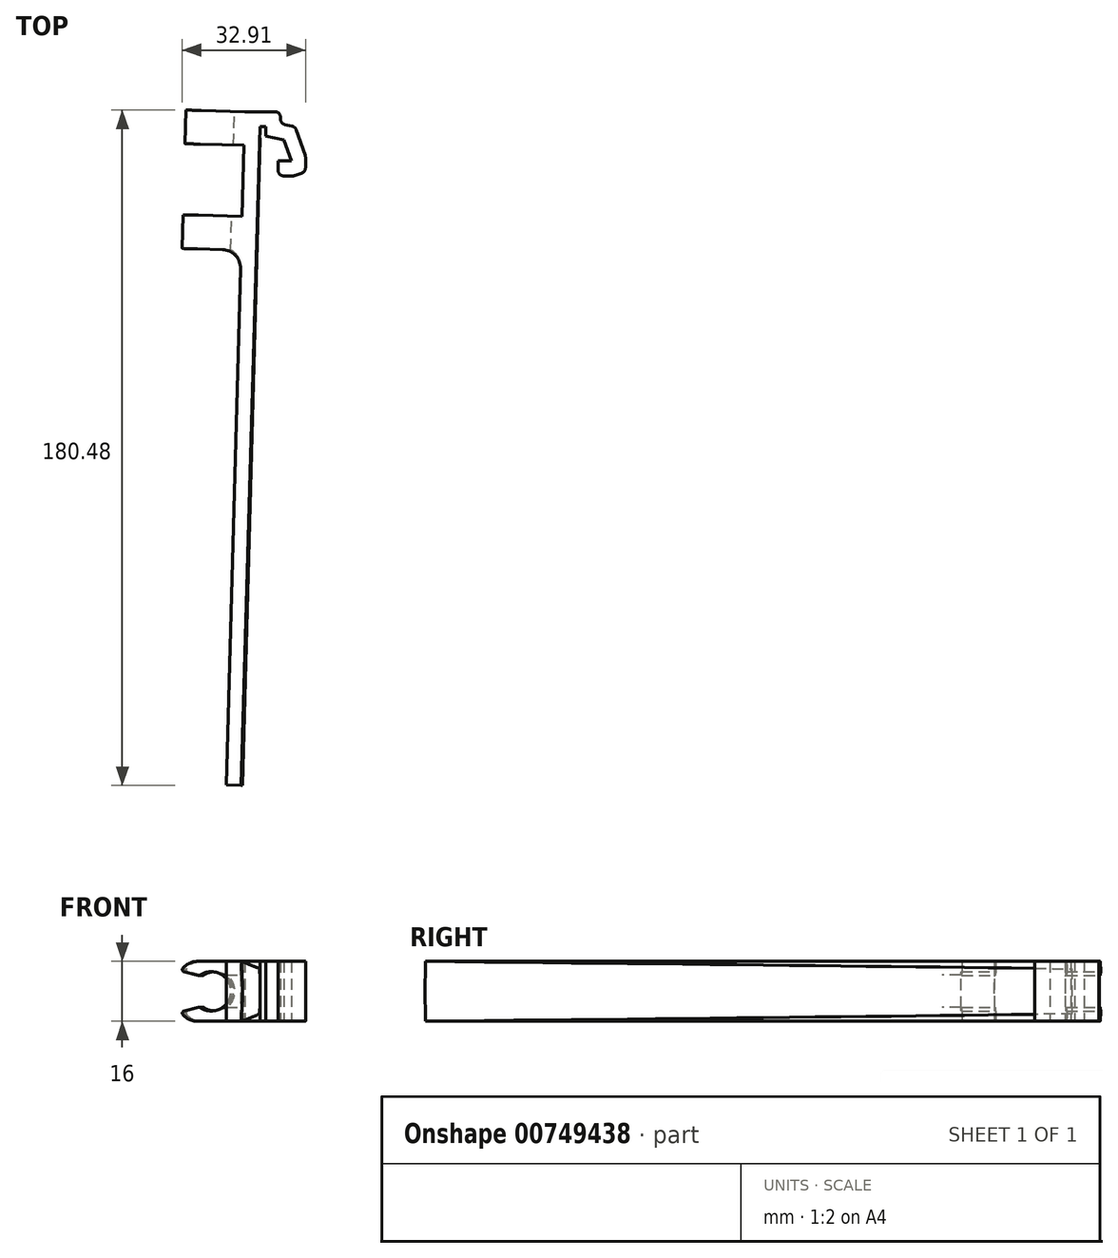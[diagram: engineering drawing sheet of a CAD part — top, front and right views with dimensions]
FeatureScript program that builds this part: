
annotation { "Feature Type Name" : "Feature", "Feature Type Description" : "" }
export const myFeature = defineFeature(function(context is Context, id is Id, definition is map)
    precondition{}
    {
        {
            var Q0;
            Q0=qCreatedBy(makeId("Top.planeOp"),FACE);
            var sketch = newSketch(context, id + "F0", { "sketchPlane" : qUnion([Q0])});
            skLineSegment(sketch, "E0", {"start": v(1.5, 0) * mm, "end": v(1.5, 2.5) * mm});
            skLineSegment(sketch, "E1", {"start": v(1.5, 2.5) * mm, "end": v(0, 2.5) * mm});
            skPoint(sketch, "E2", {"position": v(6.4, -1) * mm});
            skLineSegment(sketch, "E3", {"start": v(1.5, 0) * mm, "end": v(6.4, -1) * mm});
            skLineSegment(sketch, "E4", {"start": v(8.4, -7.43) * mm, "end": v(8.4, -1) * mm, "construction": true});
            skLineSegment(sketch, "E5", {"start": v(6.4, -1) * mm, "end": v(8.4, -6.66) * mm});
            skLineSegment(sketch, "E6.0", {"start": v(9.42, 2.47) * mm, "end": v(12.17, -5.32) * mm});
            skLineSegment(sketch, "E6.2", {"start": v(5.5, 6.5) * mm, "end": v(-4.03, 6.5) * mm});
            skLineSegment(sketch, "E6.3", {"start": v(5.5, 3.27) * mm, "end": v(5.5, 6.5) * mm});
            skLineSegment(sketch, "E6.4", {"start": v(5.5, 3.27) * mm, "end": v(9.42, 2.47) * mm});
            skLineSegment(sketch, "E7", {"start": v(1.5, 0) * mm, "end": v(1.5, -9.75) * mm, "construction": true});
            skLineSegment(sketch, "E8", {"start": v(8.4, -6.66) * mm, "end": v(6.33, -6.66) * mm});
            skLineSegment(sketch, "E9.0", {"start": v(9.09, -10.66) * mm, "end": v(6.33, -10.66) * mm});
            skLineSegment(sketch, "E9.1", {"start": v(9.09, -10.66) * mm, "end": v(12.17, -9.57) * mm});
            skLineSegment(sketch, "E10", {"start": v(12.17, -5.32) * mm, "end": v(12.17, -9.57) * mm});
            skLineSegment(sketch, "E11", {"start": v(0, 27.06) * mm, "end": v(0, -19.04) * mm, "construction": true});
            skLineSegment(sketch, "E12", {"start": v(-104, 32.98) * mm, "end": v(-104, -15.05) * mm, "construction": true});
            skLineSegment(sketch, "E13", {"start": v(-104, -15.05) * mm, "end": v(-104, -177.8) * mm, "construction": true});
            skLineSegment(sketch, "E14", {"start": v(-9, -173.43) * mm, "end": v(-5, -173.54) * mm});
            skLineSegment(sketch, "E15", {"start": v(-9, -173.43) * mm, "end": v(-4.03, 6.5) * mm});
            skLineSegment(sketch, "E16", {"start": v(-5, -173.54) * mm, "end": v(0, 2.5) * mm});
            skLineSegment(sketch, "E17.bottom", {"start": v(6.33, -6.66) * mm, "end": v(4.83, -6.66) * mm});
            skLineSegment(sketch, "E17.right", {"start": v(4.83, -6.66) * mm, "end": v(4.83, -10.66) * mm});
            skLineSegment(sketch, "E18", {"start": v(6.33, -10.66) * mm, "end": v(4.83, -10.66) * mm});
            skSolve(sketch);
        }
        {
            var Q0;
            Q0=makeQuery(id+"F0.imprint","IMPRINT",FACE,{"disambiguationData":[TD([[makeQuery(id+"F0.imprint","IMPRINT",EDGE,{"derivedFrom":sQuery(id+"F0.wireOp",EDGE,"E0")}),-1.0]])]});
            extrude(context, id + "F1", {"entities" : qUnion([Q0]), "depth" : 16 * mm, "offsetDistance" : 25 * mm});
        }
        {
            var Q0;
            Q0=makeQuery(id+"F1.opExtrude","SWEPT_FACE",FACE,{"disambiguationData":[OSD([sQuery(id+"F0.wireOp",EDGE,"E14")])]});
            var sketch = newSketch(context, id + "F2", { "sketchPlane" : qUnion([Q0])});
            skPoint(sketch, "E19", {"position": v(-4.2, 8) * mm});
            skArc(sketch, "E20", {"start": v(-0.2, 0) * mm, "mid": v(0.1, 8) * mm, "end": v(-0.2, 16) * mm});
            skLineSegment(sketch, "E21", {"start": v(-0.2, 16) * mm, "end": v(-4.2, 16) * mm});
            skLineSegment(sketch, "E22", {"start": v(-4.2, 16) * mm, "end": v(-4.2, 0) * mm});
            skLineSegment(sketch, "E23", {"start": v(-4.2, 0) * mm, "end": v(-0.2, 0) * mm});
            skSolve(sketch);
        }
        {
            var Q0;
            Q0=qSketchRegion(id+"F2",true);
            var Q1;
            Q1=makeQuery(id+"F2.imprint","IMPRINT",FACE,{"disambiguationData":[TD([[makeQuery(id+"F2.imprint","IMPRINT",EDGE,{"derivedFrom":sQuery(id+"F2.wireOp",EDGE,"E21")}),-1.0]])]});
            extrude(context, id + "F3", {"entities" : qUnion([Q0, Q1]), "operationType" : NewBodyOperationType.ADD, "oppositeDirection" : true, "depth" : 173 * mm, "offsetDistance" : 25 * mm});
        }
        {
            var Q0;
            Q0=makeQuery(id+"F1.opExtrude","SWEPT_FACE",FACE,{"disambiguationData":[OSD([sQuery(id+"F0.wireOp",EDGE,"E15")])]});
            var sketch = newSketch(context, id + "F4", { "sketchPlane" : qUnion([Q0])});
            skLineSegment(sketch, "E24", {"start": v(173.61, 8) * mm, "end": v(-6.39, 8) * mm, "construction": true});
            skLineSegment(sketch, "E25", {"start": v(83.61, 16) * mm, "end": v(83.61, 0) * mm, "construction": true});
            skLineSegment(sketch, "E26.bottom", {"start": v(-6.39, 16) * mm, "end": v(2.61, 16) * mm});
            skLineSegment(sketch, "E26.top", {"start": v(-6.39, 0) * mm, "end": v(2.61, 0) * mm});
            skLineSegment(sketch, "E26.left", {"start": v(-6.39, 16) * mm, "end": v(-6.39, 0) * mm});
            skLineSegment(sketch, "E26.right", {"start": v(2.61, 16) * mm, "end": v(2.61, 0) * mm});
            skLineSegment(sketch, "E27.bottom", {"start": v(21.61, 16) * mm, "end": v(30.61, 16) * mm});
            skLineSegment(sketch, "E27.top", {"start": v(21.61, 0) * mm, "end": v(30.61, 0) * mm});
            skLineSegment(sketch, "E27.left", {"start": v(21.61, 16) * mm, "end": v(21.61, 0) * mm});
            skLineSegment(sketch, "E27.right", {"start": v(30.61, 16) * mm, "end": v(30.61, 0) * mm});
            skSolve(sketch);
        }
        {
            var Q0;
            {var subQ0=sQuery(id+"F4.wireOp",EDGE,"32ca4d4b-827b-4836-91d8-99286762edac0.MirrorCS");Q0=makeQuery(id+"F4.imprint","IMPRINT",FACE,{"disambiguationData":[TD([[makeQuery(id+"F4.imprint","IMPRINT",EDGE,{"derivedFrom":subQ0}),1.0]])]});}
            var Q1;
            Q1=makeQuery(id+"F4.imprint","IMPRINT",FACE,{"disambiguationData":[TD([[makeQuery(id+"F4.imprint","IMPRINT",EDGE,{"derivedFrom":sQuery(id+"F4.wireOp",EDGE,"dd097a06-8009-4be6-aad0-c9cb191a08430.MirrorCS")}),1.0]])]});
            var Q2;
            Q2=makeQuery(id+"F4.imprint","IMPRINT",FACE,{"disambiguationData":[TD([[makeQuery(id+"F4.imprint","IMPRINT",EDGE,{"derivedFrom":sQuery(id+"F4.wireOp",EDGE,"E26.bottom")}),1.0]])]});
            var Q3;
            Q3=qSketchRegion(id+"F4",true);
            extrude(context, id + "F5", {"entities" : qUnion([Q0, Q1, Q2, Q3]), "operationType" : NewBodyOperationType.ADD, "depth" : 16 * mm, "offsetDistance" : 25 * mm});
        }
        {
            var Q0;
            Q0=makeQuery(id+"F5.opExtrude","SWEPT_FACE",FACE,{"disambiguationData":[OSD([sQuery(id+"F4.wireOp",EDGE,"E26.left")])]});
            var sketch = newSketch(context, id + "F6", { "sketchPlane" : qUnion([Q0])});
            skArc(sketch, "E28", {"start": v(15.36, 12.2) * mm, "mid": v(6.96, 8) * mm, "end": v(15.36, 3.8) * mm});
            skLineSegment(sketch, "E29", {"start": v(12.2, 13.25) * mm, "end": v(12.2, 2.75) * mm, "construction": true});
            skPoint(sketch, "E30", {"position": v(12.2, 3.8) * mm});
            skLineSegment(sketch, "E31", {"start": v(12.2, 3.8) * mm, "end": v(15.36, 3.8) * mm, "construction": true});
            skPoint(sketch, "E32", {"position": v(20.2, 2.5) * mm});
            skLineSegment(sketch, "E33", {"start": v(15.36, 3.8) * mm, "end": v(20.2, 2.5) * mm});
            skLineSegment(sketch, "E34", {"start": v(12.2, 8) * mm, "end": v(20.2, 8) * mm, "construction": true});
            skLineSegment(sketch, "E35.MirrorCS", {"start": v(15.36, 12.2) * mm, "end": v(20.2, 13.5) * mm});
            skLineSegment(sketch, "E36", {"start": v(20.2, 13.5) * mm, "end": v(20.2, 2.5) * mm});
            skSolve(sketch);
        }
        {
            var Q0;
            Q0=makeQuery(id+"F6.imprint","IMPRINT",FACE,{"disambiguationData":[TD([[makeQuery(id+"F6.imprint","IMPRINT",EDGE,{"derivedFrom":sQuery(id+"F6.wireOp",EDGE,"E28")}),1.0]])]});
            extrude(context, id + "F7", {"entities" : qUnion([Q0]), "operationType" : NewBodyOperationType.REMOVE, "endBound" : BoundingType.THROUGH_ALL, "oppositeDirection" : true, "depth" : 25 * mm, "offsetDistance" : 25 * mm});
        }
        {
            var Q0;
            Q0=makeQuery(id+"F5.opExtrude","CAP_EDGE",EDGE,{"disambiguationData":[OSD([sQuery(id+"F4.wireOp",EDGE,"E26.bottom")])],"isStart":false});
            var Q1;
            Q1=makeQuery(id+"F5.opExtrude","CAP_EDGE",EDGE,{"disambiguationData":[OSD([sQuery(id+"F4.wireOp",EDGE,"E26.top")])],"isStart":false});
            var Q2;
            Q2=makeQuery(id+"F5.opExtrude","CAP_EDGE",EDGE,{"disambiguationData":[OSD([sQuery(id+"F4.wireOp",EDGE,"E27.top")])],"isStart":false});
            var Q3;
            Q3=makeQuery(id+"F5.opExtrude","CAP_EDGE",EDGE,{"disambiguationData":[OSD([sQuery(id+"F4.wireOp",EDGE,"E27.bottom")])],"isStart":false});
            var Q4;
            Q4=makeQuery(id+"F5.opExtrude","CAP_EDGE",EDGE,{"disambiguationData":[OSD([sQuery(id+"F0.wireOp",EDGE,"E15")])],"isStart":false});
            var Q5;
            Q5=makeQuery(id+"F5.opExtrude","CAP_EDGE",EDGE,{"disambiguationData":[OSD([sQuery(id+"F4.wireOp",EDGE,"1fce7415-5c44-4202-8804-2bec5c6d53160.MirrorCS")])],"isStart":false});
            var Q6;
            Q6=makeQuery(id+"F5.opExtrude","CAP_EDGE",EDGE,{"disambiguationData":[OSD([sQuery(id+"F4.wireOp",EDGE,"dd097a06-8009-4be6-aad0-c9cb191a08430.MirrorCS")])],"isStart":false});
            var Q7;
            Q7=makeQuery(id+"F5.opExtrude","CAP_EDGE",EDGE,{"disambiguationData":[OSD([sQuery(id+"F4.wireOp",EDGE,"81fb2327-fdc6-4d19-a8aa-e33bda6622e80.MirrorCS")])],"isStart":false});
            fillet(context, id + "F8", {"entities" : qUnion([Q0, Q1, Q2, Q3, Q4, Q5, Q6, Q7]), "radius" : 5 * mm, "tangentPropagation" : true, "allowEdgeOverflow" : false});
        }
        {
            var Q0;
            Q0=makeQuery(id+"F5.opExtrude","CAP_EDGE",EDGE,{"disambiguationData":[OSD([sQuery(id+"F4.wireOp",EDGE,"45b973a7-b805-4cbf-98a5-462aa30b31510.MirrorCS")])],"isStart":true});
            var Q1;
            Q1=makeQuery(id+"F5.opExtrude","CAP_EDGE",EDGE,{"disambiguationData":[OSD([sQuery(id+"F4.wireOp",EDGE,"E27.left")])],"isStart":true});
            var Q2;
            Q2=makeQuery(id+"F5.opExtrude","CAP_EDGE",EDGE,{"disambiguationData":[OSD([sQuery(id+"F4.wireOp",EDGE,"32ca4d4b-827b-4836-91d8-99286762edac0.MirrorCS")])],"isStart":true});
            var Q3;
            Q3=makeQuery(id+"F5.opExtrude","CAP_EDGE",EDGE,{"disambiguationData":[OSD([sQuery(id+"F4.wireOp",EDGE,"E26.right")])],"isStart":true});
            var Q4;
            Q4=makeQuery(id+"F5.opExtrude","CAP_EDGE",EDGE,{"disambiguationData":[OSD([sQuery(id+"F4.wireOp",EDGE,"E27.right")])],"isStart":true});
            var Q5;
            Q5=makeQuery(id+"F5.opExtrude","CAP_EDGE",EDGE,{"disambiguationData":[OSD([sQuery(id+"F4.wireOp",EDGE,"e8549d8e-8030-4f0a-b5fa-27ac290f47030.MirrorCS")])],"isStart":true});
            fillet(context, id + "F9", {"entities" : qUnion([Q0, Q1, Q2, Q3, Q4, Q5]), "radius" : 5 * mm, "tangentPropagation" : true, "allowEdgeOverflow" : false});
        }
        {
            var Q0;
            Q0=makeQuery(id+"F1.opExtrude","SWEPT_EDGE",EDGE,{"disambiguationData":[OSD([sQuery(id+"F0.wireOp",EDGE,"E6.2"),sQuery(id+"F0.wireOp",EDGE,"E6.3")])]});
            var Q1;
            Q1=makeQuery(id+"F1.opExtrude","SWEPT_EDGE",EDGE,{"disambiguationData":[OSD([sQuery(id+"F0.wireOp",EDGE,"E6.3"),sQuery(id+"F0.wireOp",EDGE,"E6.4")])]});
            var Q2;
            Q2=makeQuery(id+"F1.opExtrude","SWEPT_EDGE",EDGE,{"disambiguationData":[OSD([sQuery(id+"F0.wireOp",EDGE,"E6.0"),sQuery(id+"F0.wireOp",EDGE,"E6.4")])]});
            var Q3;
            Q3=makeQuery(id+"F1.opExtrude","SWEPT_EDGE",EDGE,{"disambiguationData":[OSD([sQuery(id+"F0.wireOp",EDGE,"E6.0"),sQuery(id+"F0.wireOp",EDGE,"E10")])]});
            var Q4;
            Q4=makeQuery(id+"F1.opExtrude","SWEPT_EDGE",EDGE,{"disambiguationData":[OSD([sQuery(id+"F0.wireOp",EDGE,"E9.1"),sQuery(id+"F0.wireOp",EDGE,"E10")])]});
            var Q5;
            Q5=makeQuery(id+"F1.opExtrude","SWEPT_EDGE",EDGE,{"disambiguationData":[OSD([sQuery(id+"F0.wireOp",EDGE,"E9.0"),sQuery(id+"F0.wireOp",EDGE,"E9.1")])]});
            var Q6;
            Q6=makeQuery(id+"F1.opExtrude","SWEPT_EDGE",EDGE,{"disambiguationData":[OSD([sQuery(id+"F0.wireOp",EDGE,"E17.right"),sQuery(id+"F0.wireOp",EDGE,"E18")])]});
            fillet(context, id + "F10", {"entities" : qUnion([Q0, Q1, Q2, Q3, Q4, Q5, Q6]), "radius" : 1.5 * mm, "tangentPropagation" : true, "allowEdgeOverflow" : false});
        }
        {
            var Q0;
            {var subQ0=sQuery(id+"F6.wireOp",EDGE,"E28");var subQ1=sQuery(id+"F6.wireOp",EDGE,"E35.MirrorCS");Q0=makeQuery(id+"F7.boolean.opBoolean","COPY",EDGE,{"disambiguationData":[TD([makeQuery(id+"F5.opExtrude","SWEPT_FACE",FACE,{"disambiguationData":[OSD([sQuery(id+"F4.wireOp",EDGE,"E26.left")])]})])],"derivedFrom":makeQuery(id+"F7.opExtrude","SWEPT_EDGE",EDGE,{"disambiguationData":[OSD([subQ0,subQ1])]})});}
            var Q1;
            {var subQ1=sQuery(id+"F4.wireOp",EDGE,"E26.left");var subQ2=sQuery(id+"F4.wireOp",EDGE,"E26.top");Q1=makeQuery(id+"F8.opFillet","BLEND_EDGE",EDGE,{"blendedFrom":[makeQuery(id+"F5.opExtrude","CAP_EDGE",EDGE,{"disambiguationData":[OSD([subQ2])],"isStart":false}),makeQuery(id+"F7.boolean.opBoolean","COPY",FACE,{"disambiguationData":[TD([makeQuery(id+"F5.opExtrude","SWEPT_FACE",FACE,{"disambiguationData":[OSD([subQ1])]})])],"derivedFrom":makeQuery(id+"F7.opExtrude","SWEPT_FACE",FACE,{"disambiguationData":[OSD([sQuery(id+"F6.wireOp",EDGE,"E33")])]})})],"blendedInto":[makeQuery(id+"F7.boolean.opBoolean","COPY",FACE,{"disambiguationData":[TD([makeQuery(id+"F5.opExtrude","SWEPT_FACE",FACE,{"disambiguationData":[OSD([subQ1])]})])],"derivedFrom":makeQuery(id+"F7.opExtrude","SWEPT_FACE",FACE,{"disambiguationData":[OSD([sQuery(id+"F6.wireOp",EDGE,"E33")])]})})]});}
            var Q2;
            {var subQ0=sQuery(id+"F6.wireOp",EDGE,"E28");var subQ1=sQuery(id+"F6.wireOp",EDGE,"E33");Q2=makeQuery(id+"F7.boolean.opBoolean","COPY",EDGE,{"disambiguationData":[TD([makeQuery(id+"F5.opExtrude","SWEPT_FACE",FACE,{"disambiguationData":[OSD([sQuery(id+"F4.wireOp",EDGE,"E27.left")])]})])],"derivedFrom":makeQuery(id+"F7.opExtrude","SWEPT_EDGE",EDGE,{"disambiguationData":[OSD([subQ0,subQ1])]})});}
            var Q3;
            {var subQ0=sQuery(id+"F6.wireOp",EDGE,"E28");var subQ1=sQuery(id+"F6.wireOp",EDGE,"E35.MirrorCS");Q3=makeQuery(id+"F7.boolean.opBoolean","COPY",EDGE,{"disambiguationData":[TD([makeQuery(id+"F5.opExtrude","SWEPT_FACE",FACE,{"disambiguationData":[OSD([sQuery(id+"F4.wireOp",EDGE,"E27.left")])]})])],"derivedFrom":makeQuery(id+"F7.opExtrude","SWEPT_EDGE",EDGE,{"disambiguationData":[OSD([subQ0,subQ1])]})});}
            var Q4;
            {var subQ1=sQuery(id+"F4.wireOp",EDGE,"E26.left");var subQ2=sQuery(id+"F4.wireOp",EDGE,"E26.bottom");Q4=makeQuery(id+"F8.opFillet","BLEND_EDGE",EDGE,{"blendedFrom":[makeQuery(id+"F5.opExtrude","CAP_EDGE",EDGE,{"disambiguationData":[OSD([subQ2])],"isStart":false}),makeQuery(id+"F7.boolean.opBoolean","COPY",FACE,{"disambiguationData":[TD([makeQuery(id+"F5.opExtrude","SWEPT_FACE",FACE,{"disambiguationData":[OSD([subQ1])]})])],"derivedFrom":makeQuery(id+"F7.opExtrude","SWEPT_FACE",FACE,{"disambiguationData":[OSD([sQuery(id+"F6.wireOp",EDGE,"E35.MirrorCS")])]})})],"blendedInto":[makeQuery(id+"F7.boolean.opBoolean","COPY",FACE,{"disambiguationData":[TD([makeQuery(id+"F5.opExtrude","SWEPT_FACE",FACE,{"disambiguationData":[OSD([subQ1])]})])],"derivedFrom":makeQuery(id+"F7.opExtrude","SWEPT_FACE",FACE,{"disambiguationData":[OSD([sQuery(id+"F6.wireOp",EDGE,"E35.MirrorCS")])]})})]});}
            var Q5;
            {var subQ0=sQuery(id+"F6.wireOp",EDGE,"E28");var subQ1=sQuery(id+"F6.wireOp",EDGE,"E33");Q5=makeQuery(id+"F7.boolean.opBoolean","COPY",EDGE,{"disambiguationData":[TD([makeQuery(id+"F5.opExtrude","SWEPT_FACE",FACE,{"disambiguationData":[OSD([sQuery(id+"F4.wireOp",EDGE,"E26.left")])]})])],"derivedFrom":makeQuery(id+"F7.opExtrude","SWEPT_EDGE",EDGE,{"disambiguationData":[OSD([subQ0,subQ1])]})});}
            var Q6;
            {var subQ1=sQuery(id+"F4.wireOp",EDGE,"E27.left");var subQ2=sQuery(id+"F4.wireOp",EDGE,"E27.bottom");Q6=makeQuery(id+"F8.opFillet","BLEND_EDGE",EDGE,{"blendedFrom":[makeQuery(id+"F5.opExtrude","CAP_EDGE",EDGE,{"disambiguationData":[OSD([subQ2])],"isStart":false}),makeQuery(id+"F7.boolean.opBoolean","COPY",FACE,{"disambiguationData":[TD([makeQuery(id+"F5.opExtrude","SWEPT_FACE",FACE,{"disambiguationData":[OSD([subQ1])]})])],"derivedFrom":makeQuery(id+"F7.opExtrude","SWEPT_FACE",FACE,{"disambiguationData":[OSD([sQuery(id+"F6.wireOp",EDGE,"E35.MirrorCS")])]})})],"blendedInto":[makeQuery(id+"F7.boolean.opBoolean","COPY",FACE,{"disambiguationData":[TD([makeQuery(id+"F5.opExtrude","SWEPT_FACE",FACE,{"disambiguationData":[OSD([subQ1])]})])],"derivedFrom":makeQuery(id+"F7.opExtrude","SWEPT_FACE",FACE,{"disambiguationData":[OSD([sQuery(id+"F6.wireOp",EDGE,"E35.MirrorCS")])]})})]});}
            var Q7;
            {var subQ1=sQuery(id+"F4.wireOp",EDGE,"E27.left");var subQ2=sQuery(id+"F4.wireOp",EDGE,"E27.top");Q7=makeQuery(id+"F8.opFillet","BLEND_EDGE",EDGE,{"blendedFrom":[makeQuery(id+"F5.opExtrude","CAP_EDGE",EDGE,{"disambiguationData":[OSD([subQ2])],"isStart":false}),makeQuery(id+"F7.boolean.opBoolean","COPY",FACE,{"disambiguationData":[TD([makeQuery(id+"F5.opExtrude","SWEPT_FACE",FACE,{"disambiguationData":[OSD([subQ1])]})])],"derivedFrom":makeQuery(id+"F7.opExtrude","SWEPT_FACE",FACE,{"disambiguationData":[OSD([sQuery(id+"F6.wireOp",EDGE,"E33")])]})})],"blendedInto":[makeQuery(id+"F7.boolean.opBoolean","COPY",FACE,{"disambiguationData":[TD([makeQuery(id+"F5.opExtrude","SWEPT_FACE",FACE,{"disambiguationData":[OSD([subQ1])]})])],"derivedFrom":makeQuery(id+"F7.opExtrude","SWEPT_FACE",FACE,{"disambiguationData":[OSD([sQuery(id+"F6.wireOp",EDGE,"E33")])]})})]});}
            fillet(context, id + "F11", {"entities" : qUnion([Q0, Q1, Q2, Q3, Q4, Q5, Q6, Q7]), "radius" : 0.5 * mm, "tangentPropagation" : true, "allowEdgeOverflow" : false});
        }
    });
